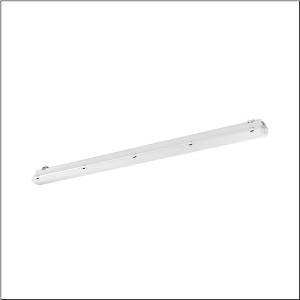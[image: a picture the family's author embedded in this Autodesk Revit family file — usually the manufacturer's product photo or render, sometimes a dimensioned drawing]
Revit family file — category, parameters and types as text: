
# Revit family: monsun_r__11xtreme_mo_51fe10mp480r_a813
name_source: partatom
category: Lighting Fixtures
units: mm (PartAtom-declared; Revit-internal decimal feet)

## family parameters
Cut with Voids When Loaded = No
Host = Face
Light Source = No
Part Type = Normal
Room Calculation Point = No
Round Connector Dimension = Use Diameter
Shared = No

## types (1)
- --- (1 x LED, 8000 lm, 43.2 W, 4000K)
    Apparent Load = 43 VA
    CIE Flux Codes = 47 77 93 94 100
    Color Rendering = 80
    Color Temperature = 4000K
    Default Elevation = 1800 mm
    Description = Monsun® 11Xtreme MO, damp-proof luminaire, chain hanger, primary optical cover: enclosure, of PMMA, light emission: direct distribution, primary light characteristic: symmetric, installation type: suspended mounting, surface-mounted, horizontal mounting, vertical mounting, LED, rated luminous flux: 8.000lm, luminous efficacy: 181lm/W, light colour: 840, colour temperature: 4000K, control gear: ECG, with terminal, 3-pole, max. 2.5mm², mains connection: 220..240V, AC, 50/60Hz, rated input power: 44W, luminaire housing, of glass-fibre reinforced polyester, uncoated, bright grey, incl. chain hanger, length: 1.590mm, width: 90mm, height: 88mm, clip for enclosure, of stainless steel (V2A), ceiling mounting element, of stainless steel (V2A), chain hanger, of stainless steel (V2A), protection rating (complete): IP66, insulation class (complete): insulation class I (protective earthing), certification: CE, ENEC, VDE, UKCA, protection symbol: D, impact resistance: IK04, permissible operating ambient temperature: -35..+55°C (at 8000lm) / 60°C (at 4100lm), standard: EN 50419, EN 60598-2-1, corresponds to IFS (International Featured Standards) requirements for safety and quality in the food industry, for indoor or canopied outdoor use, no direct snow, no direct sun, no direct rain, contact your sales advisor before using the luminaires in applications with unclear chemical exposure, large temperature fluctuations or condensation-forming humidity, LABS conformity tested according to VDMA 24364:2018-05, packaging unit: 1 piece
    Height = 88 mm
    Lamp = 1 x LED
    Lamp Light Flux = 8000 lm
    Lamp Power = 43.2 W
    Lamp count = 1
    Length = 1590 mm
    Luminous efficacy = 185 lm/W
    Manufacturer = Siteco
    ModVariant = No
    Model = 51FE10MP480R
    Mounting Place = Ceiling
    Mounting Type = Surface mounted
    Number of Poles = 1
    OnlyDefault = Yes
    Power Factor = 1
    Product Name = Monsun® 11Xtreme MO
    Product group = damp-proof luminaire
    ProductGroupID = 300
    Protection Class = Protection class I
    Protection Degree = IP 66
    RLX_Detail_Level = 1
    RLX_Emergency_Light_Flux = 0 lm
    RLX_Emergency_Type = 0
    RLX_Emergency_Type_DB = No
    RlxData = <blob elided: 85341 chars, md5=97589e4b>
    Socket = socket
    Standby Power = 0 W
    System Light Flux = 8000 lm
    System Power = 43 W
    Type Comments = factory setting: luminous flux: 100 % | (A | C | E) | 101 mA
    Type Image = l_1006851.jpg
    URL = http://relux.com
    VarID = @adj_126517
    Voltage = 0 V
    Weight = 0.00 kg
    Width = 90 mm

## geometry (parser evidence)
native form markers: Blend x4, Sweep x12
no freeform markers — native parametric forms only
